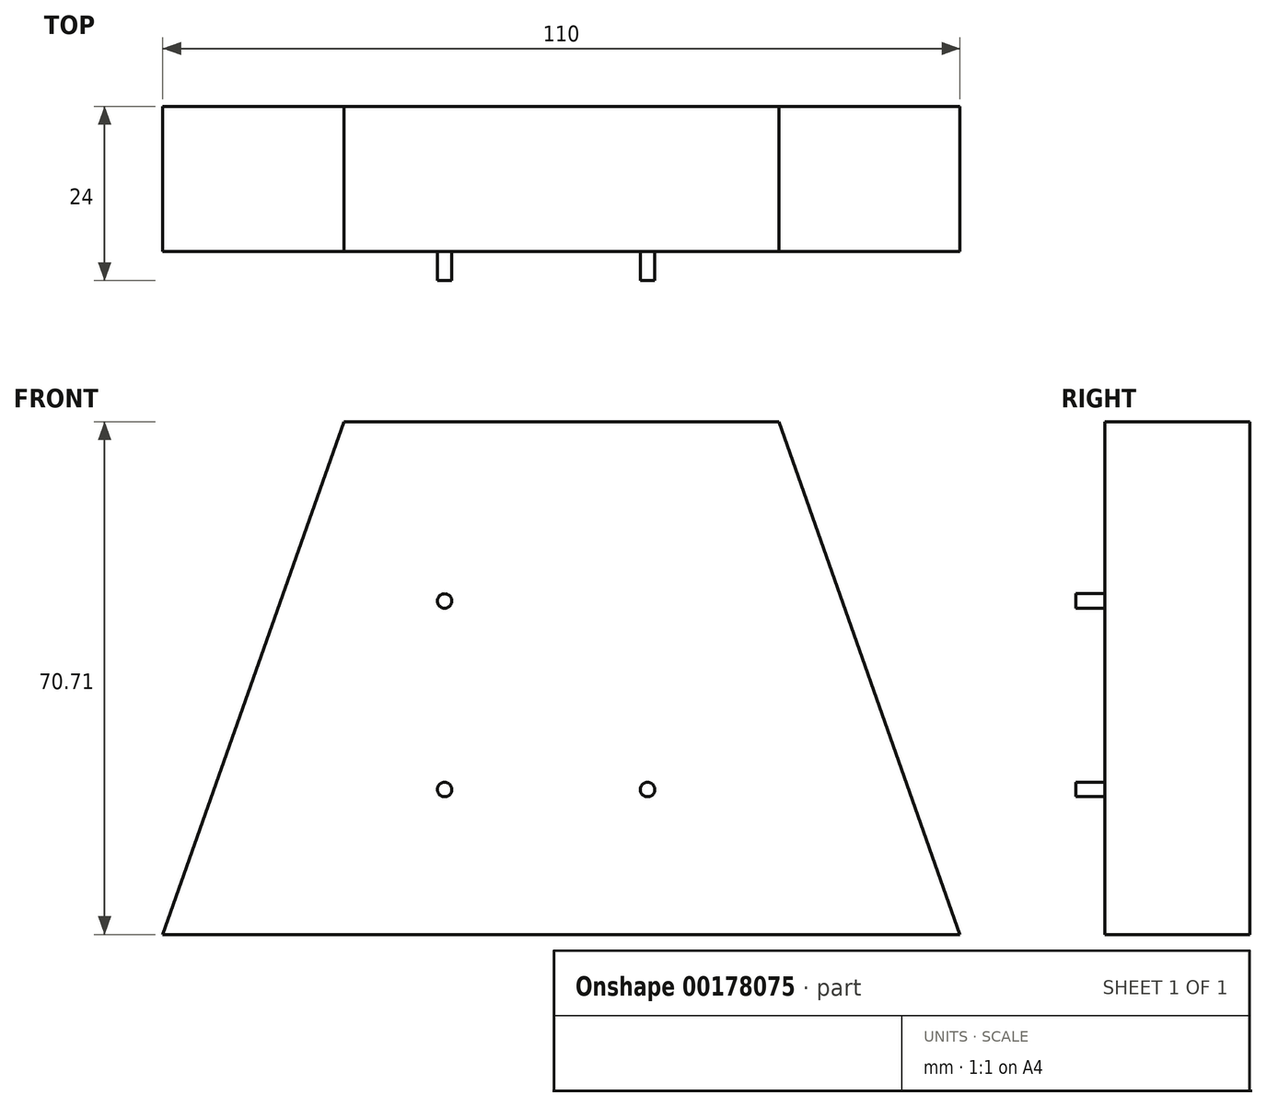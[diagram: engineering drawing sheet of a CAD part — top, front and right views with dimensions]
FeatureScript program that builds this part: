
annotation { "Feature Type Name" : "Feature", "Feature Type Description" : "" }
export const myFeature = defineFeature(function(context is Context, id is Id, definition is map)
    precondition{}
    {
        {
            var Q0;
            Q0=qCreatedBy(makeId("Front.planeOp"),FACE);
            var sketch = newSketch(context, id + "F0", { "sketchPlane" : qUnion([Q0])});
            skLineSegment(sketch, "E0", {"start": v(0, 32.44) * mm, "end": v(-30, 32.44) * mm});
            skLineSegment(sketch, "E1", {"start": v(-30, 32.44) * mm, "end": v(-55, -38.27) * mm});
            skLineSegment(sketch, "E2", {"start": v(-55, -38.27) * mm, "end": v(0, -38.27) * mm});
            skLineSegment(sketch, "E3", {"start": v(0, 32.44) * mm, "end": v(0, -38.27) * mm, "construction": true});
            skLineSegment(sketch, "E4.MirrorCS", {"start": v(0, 32.44) * mm, "end": v(30, 32.44) * mm});
            skLineSegment(sketch, "E5.MirrorCS", {"start": v(30, 32.44) * mm, "end": v(55, -38.27) * mm});
            skLineSegment(sketch, "E6.MirrorCS", {"start": v(55, -38.27) * mm, "end": v(0, -38.27) * mm});
            skSolve(sketch);
        }
        {
            var Q0;
            Q0 = qSketchRegion(id + "F0", true);
            extrude(context, id + "F1", {"entities" : qUnion([Q0]), "depth" : 20 * mm});
        }
        {
            var Q0;
            Q0=makeQuery(id+"F1.opExtrude","CAP_FACE",FACE,{"disambiguationData":[OSD([sQuery(id+"F0.wireOp",EDGE,"E0"),sQuery(id+"F0.wireOp",EDGE,"E1"),sQuery(id+"F0.wireOp",EDGE,"E2"),sQuery(id+"F0.wireOp",EDGE,"E4.MirrorCS"),sQuery(id+"F0.wireOp",EDGE,"E5.MirrorCS"),sQuery(id+"F0.wireOp",EDGE,"E6.MirrorCS")])],"isStart":false});
            var sketch = newSketch(context, id + "F2", { "sketchPlane" : qUnion([Q0])});
            skCircle(sketch, "E7", {"center": v(-16.1, 7.73) * mm, "radius": 1 * mm});
            skCircle(sketch, "E8", {"center": v(-16.1, -18.27) * mm, "radius": 1 * mm});
            skCircle(sketch, "E9", {"center": v(11.9, -18.27) * mm, "radius": 1 * mm});
            skSolve(sketch);
        }
        {
            var Q0;
            Q0 = qSketchRegion(id + "F2", true);
            extrude(context, id + "F3", {"entities" : qUnion([Q0]), "operationType" : NewBodyOperationType.ADD, "depth" : 4 * mm});
        }
    });
